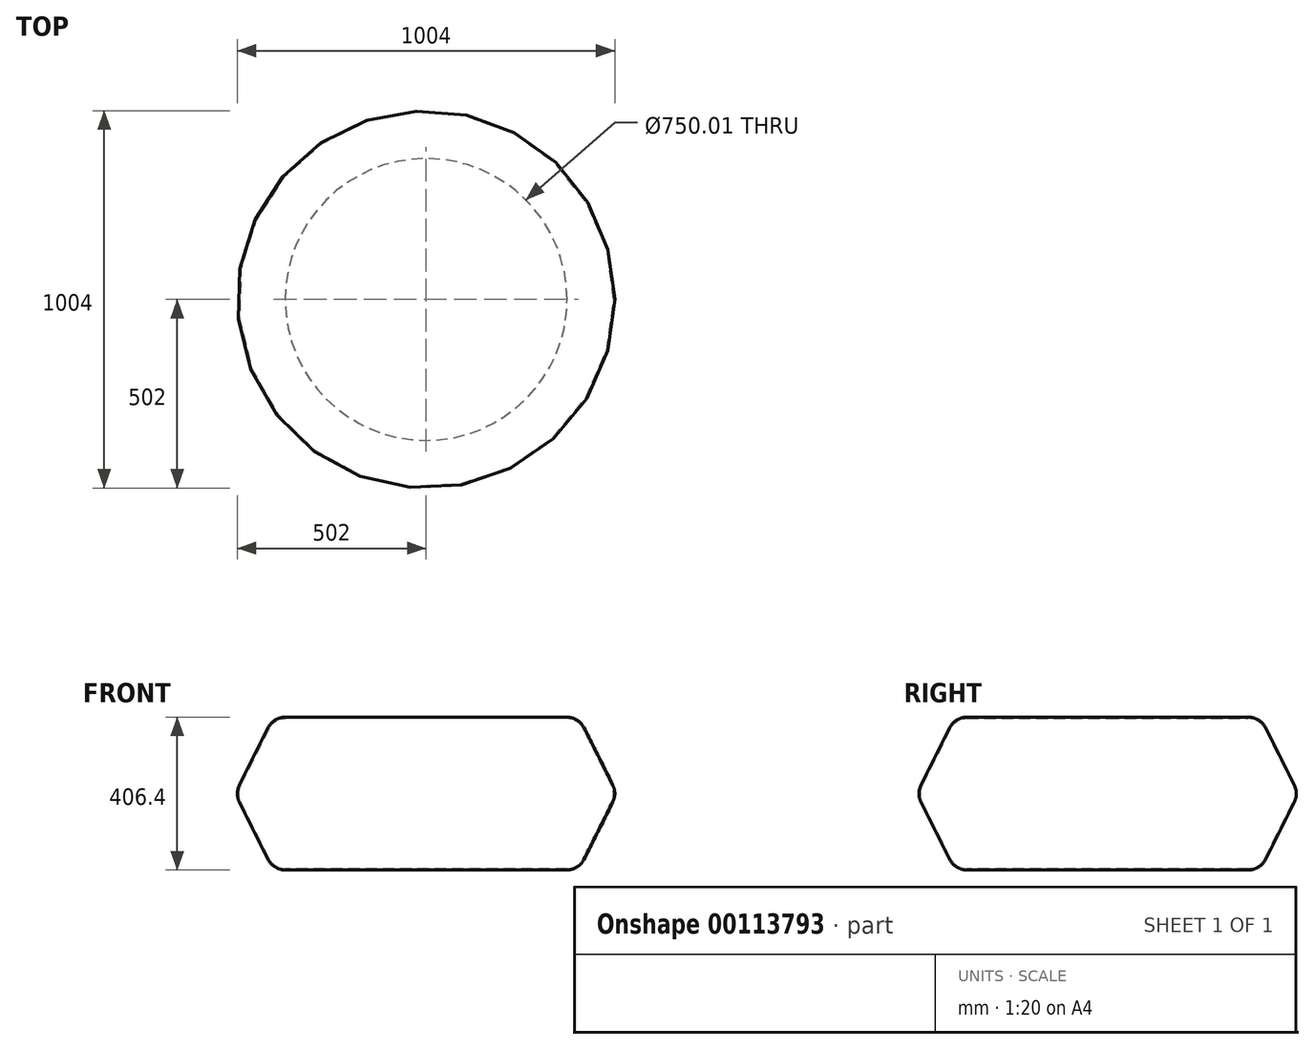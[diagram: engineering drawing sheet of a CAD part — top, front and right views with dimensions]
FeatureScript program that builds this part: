
annotation { "Feature Type Name" : "Feature", "Feature Type Description" : "" }
export const myFeature = defineFeature(function(context is Context, id is Id, definition is map)
    precondition{}
    {
        {
            var Q0;
            Q0=qCreatedBy(makeId("Front.planeOp"),FACE);
            var sketch = newSketch(context, id + "F0", { "sketchPlane" : qUnion([Q0])});
            skLineSegment(sketch, "E0.bottom", {"start": v(375, -203.2) * mm, "end": v(-406.4, -203.2) * mm, "construction": true});
            skLineSegment(sketch, "E0.left", {"start": v(406.4, -203.2) * mm, "end": v(406.4, 197.1) * mm, "construction": true});
            skLineSegment(sketch, "E0.right", {"start": v(-406.4, -203.2) * mm, "end": v(-406.4, 203.2) * mm});
            skPoint(sketch, "E0.middle", {"position": v(0, 0) * mm});
            skLineSegment(sketch, "E1", {"start": v(0, 0) * mm, "end": v(508, 0) * mm, "construction": true});
            skPoint(sketch, "E1.endSnap0", {"position": v(406.4, 0) * mm});
            skLineSegment(sketch, "E2", {"start": v(420.44, 175.12) * mm, "end": v(496.64, 22.72) * mm});
            skLineSegment(sketch, "E3", {"start": v(420.44, -175.12) * mm, "end": v(496.64, -22.72) * mm});
            skPoint(sketch, "E4.visualSharp", {"position": v(508, 0) * mm});
            skArc(sketch, "E4.filletArc", {"start": v(496.64, -22.72) * mm, "mid": v(502, 0) * mm, "end": v(496.64, 22.72) * mm});
            skPoint(sketch, "E5.visualSharp", {"position": v(406.4, 203.2) * mm});
            skPoint(sketch, "E6.visualSharp", {"position": v(406.4, -203.2) * mm});
            skArc(sketch, "E6.filletArc", {"start": v(375, -203.2) * mm, "mid": v(401.71, -195.61) * mm, "end": v(420.44, -175.12) * mm});
            skLineSegment(sketch, "E7", {"start": v(0, 203.2) * mm, "end": v(0, -203.2) * mm, "construction": true});
            skLineSegment(sketch, "E8", {"start": v(0, 203.2) * mm, "end": v(375, 203.2) * mm});
            skArc(sketch, "E9.0", {"start": v(375, -200.47) * mm, "mid": v(400.28, -193.3) * mm, "end": v(418, -173.9) * mm});
            skLineSegment(sketch, "E9.1", {"start": v(418, -173.9) * mm, "end": v(494.2, -21.5) * mm});
            skLineSegment(sketch, "E9.2", {"start": v(0, 200.47) * mm, "end": v(373.32, 200.47) * mm});
            skLineSegment(sketch, "E9.4", {"start": v(418.75, 172.39) * mm, "end": v(494.2, 21.5) * mm});
            skArc(sketch, "E9.5", {"start": v(494.2, -21.5) * mm, "mid": v(499.27, 0) * mm, "end": v(494.2, 21.5) * mm});
            skLineSegment(sketch, "E10", {"start": v(0, 200.47) * mm, "end": v(0, 203.2) * mm});
            skLineSegment(sketch, "E11", {"start": v(375, -200.47) * mm, "end": v(375, -203.2) * mm});
            skPoint(sketch, "E12.visualSharp", {"position": v(404.71, 200.47) * mm});
            skArc(sketch, "E12.filletArc", {"start": v(418.75, 172.39) * mm, "mid": v(400.02, 192.88) * mm, "end": v(373.32, 200.47) * mm});
            skArc(sketch, "E13.filletArc", {"start": v(420.44, 175.12) * mm, "mid": v(401.71, 195.61) * mm, "end": v(375, 203.2) * mm});
            skSolve(sketch);
        }
        {
            var Q0;
            Q0 = qSketchRegion(id + "F0", true);
            var Q1;
            Q1=sQuery(id+"F0.wireOp",EDGE,"E7");
            revolve(context, id + "F1", {"entities" : qUnion([Q0]), "axis" : qUnion([Q1]), "revolveType" : RevolveType.FULL});
        }
    });
